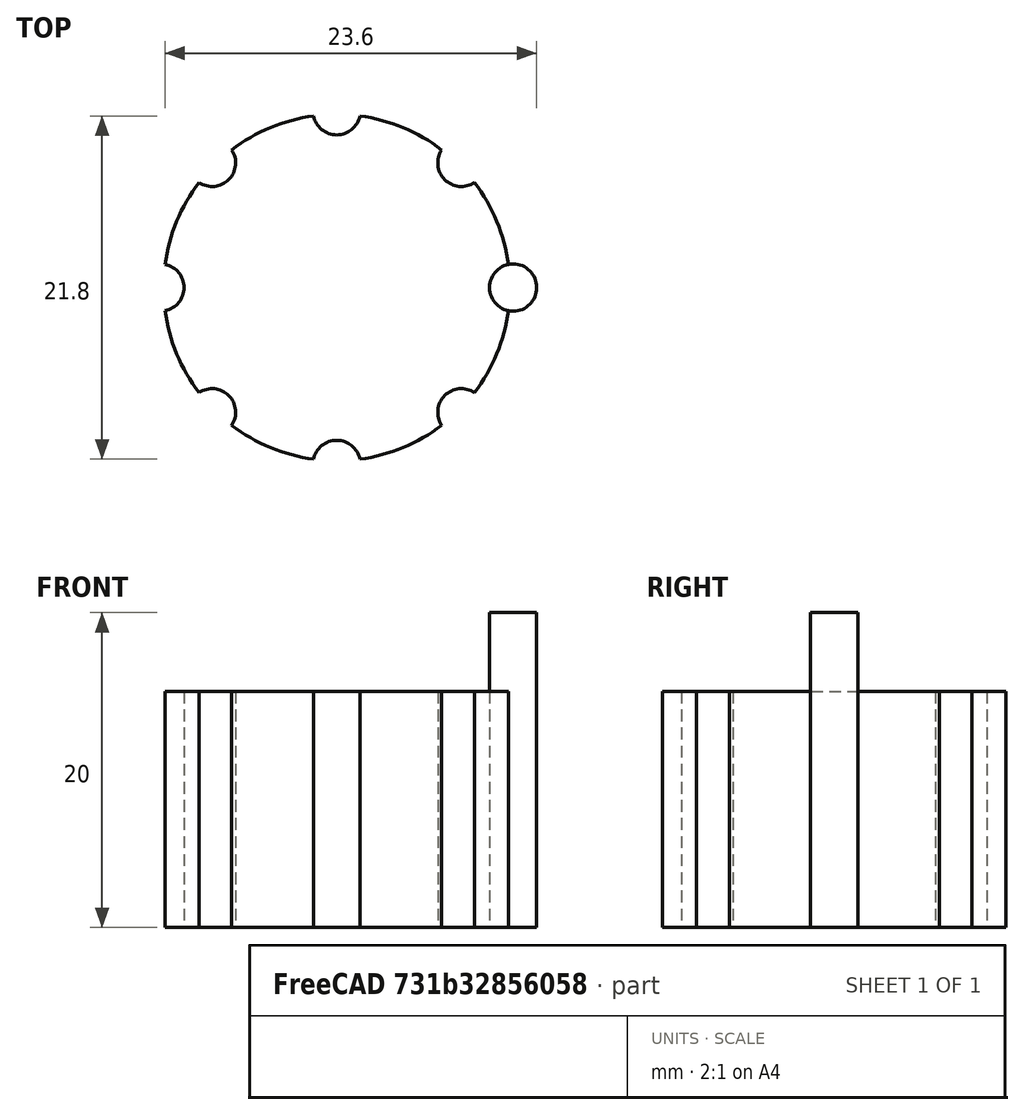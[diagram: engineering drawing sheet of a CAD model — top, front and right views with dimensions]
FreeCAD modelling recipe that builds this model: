
FCSTD DOCUMENT  (FreeCAD 1.0R39319 (Git))
Label: ojt1_t11r01_buttom
License: All rights reserved
LicenseURL: https://en.wikipedia.org/wiki/All_rights_reserved
objects: Part::Cylinder×2, Part::FeaturePython×1, Part::Cut×1
note: 3 computed .brp shape members not serialized (recipe doc carries the construction recipe); baked Part::Feature solids carry a one-line shape summary decoded from their .brp

FEATURE [Part::Cylinder] Cylinder  label="base"
  Angle = 360
  AttacherType = Attacher::AttachEngine3D
  FirstAngle = 0
  Height = 15
  Radius = 11
  SecondAngle = 0
FEATURE [Part::Cylinder] Cylinder001  label="Cilindre"
  Angle = 360
  AttacherType = Attacher::AttachEngine3D
  FirstAngle = 0
  Height = 20
  Placement = pos=(11.2,0,0) rot=(0,0,1;0rad)
  Radius = 1.5
  SecondAngle = 0
FEATURE [Part::FeaturePython] Array  # Draft array (typed FeaturePython)
  AlwaysSyncPlacement = false
  Angle = 360
  ArrayType = 1
  Axis = (0,0,1)
  Base = -> Cylinder001
  Center = (0,0,0)
  Count = 8
  ExpandArray = false
  Fuse = false
  IntervalAxis = (0,0,0)
  IntervalX = (100,0,0)
  IntervalY = (0,100,0)
  IntervalZ = (0,0,100)
  NumberCircles = 3
  NumberPolar = 8
  NumberX = 2
  NumberY = 2
  NumberZ = 1
  PlacementList = 8 placements: [(11.2,0,0),(7.9196,7.9196,0),(0,11.2,0),(-7.9196,7.9196,0),(-11.2,1.3716e-15,0),(-7.9196,-7.9196,0),(-2.4869e-15,-11.2,0),(7.9196,-7.9196,0)]
  RadialDistance = 50
  ScaleList = (8) [(1,1,1),(1,1,1),(1,1,1),(1,1,1),(1,1,1),(1,1,1),(1,1,1),(1,1,1)]
  Symmetry = 1
  TangentialDistance = 25
FEATURE [Part::Cut] Cut
  Base = -> Cylinder
  Tool = -> Array
